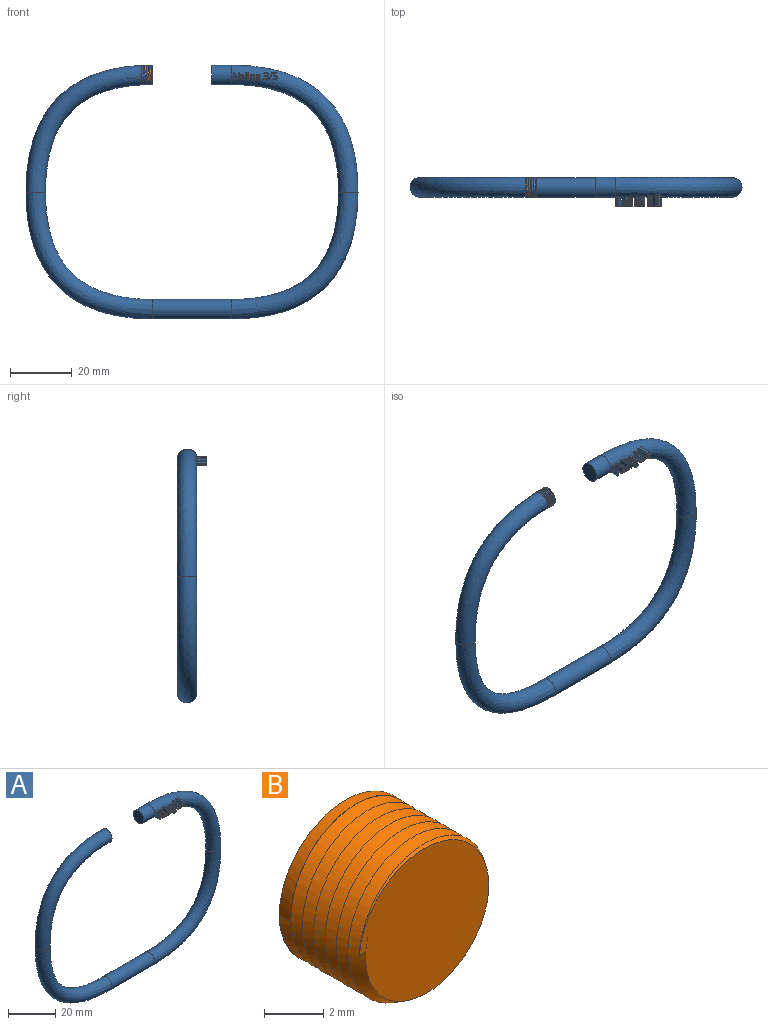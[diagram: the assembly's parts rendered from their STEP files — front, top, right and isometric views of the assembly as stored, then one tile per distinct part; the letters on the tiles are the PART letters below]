
ASSEMBLY  parts=2 mates=1
PART A: 201 faces, bbox 108x12.7x82.6 mm
  f0: bspline ~41.28x41.28mm, area 1222.4mm2, adj f3,f4,f12,f13,f14,f15,f16,f17
  f1: plane 6.35x6.35mm, normal (-1,0,0), area 31.7mm2, adj f3
  f2: plane 6.35x6.35mm, normal (1,0,0), area 31.7mm2, adj f7
  f3: cylinder r=3.17mm len=6.35mm, axis (1,0,0), area 126.7mm2, adj f0,f1
  f4: bspline ~41.28x41.28mm, area 1233.9mm2, adj f0,f5
  f5: cylinder r=3.17mm len=25.4mm, axis (-1,0,0), area 506.7mm2, adj f4,f6
  f6: bspline ~41.28x41.28mm, area 1233.9mm2, adj f5,f7
  f7: bspline ~41.28x41.28mm, area 1234.2mm2, adj f2,f6
  f8: plane 3.23x0.7mm, normal (-0.94,0,-0.35), area 2.4mm2, adj f9,f20,f21,f22
  f9: plane 3.23x0.73mm, normal (0,0,1), area 2.4mm2, adj f8,f10,f21,f22
  f10: plane 3.23x0.7mm, normal (0.94,0,-0.35), area 2.4mm2, adj f9,f11,f21,f22
  f11: extruded ~3.21x0.33mm, area 1.1mm2, adj f10,f20,f21,f22
  f12: plane 3.58x0.73mm, normal (-0.93,0,-0.36), area 2.6mm2, adj f0,f13,f19,f21
  f13: plane 3.57x0.27mm, normal (0,0,-1), area 1mm2, adj f0,f12,f14,f21
  f14: plane 3.56x2.27mm, normal (0.93,0,0.36), area 8mm2, adj f0,f13,f15,f21
  f15: plane 3.26x0.22mm, normal (0,0,1), area 0.7mm2, adj f0,f14,f16,f21
  f16: plane 3.58x2.27mm, normal (-0.93,0,0.37), area 8mm2, adj f0,f15,f17,f21
  f17: plane 3.58x0.27mm, normal (0,0,-1), area 1mm2, adj f0,f16,f18,f21
  f18: plane 3.58x0.72mm, normal (0.93,0,-0.36), area 2.6mm2, adj f0,f17,f19,f21
  f19: plane 3.29x0.91mm, normal (0,0,-1), area 3mm2, adj f0,f12,f18,f21
  f20: extruded ~3.21x0.33mm, area 1.1mm2, adj f8,f11,f21,f22
  f21: plane 2.27x2.01mm, normal (0,-1,0), area 1.3mm2, adj f8,f9,f10,f11,f12,f13,f14,f15
  f22: bspline ~6.4x6.35mm, area 0.4mm2, adj f8,f9,f10,f11,f20
  f23: plane 3.56x0.26mm, normal (0,0,-1), area 0.9mm2, adj f0,f24,f26,f27
  f24: plane 3.55x1.7mm, normal (1,0,0), area 5.6mm2, adj f0,f23,f25,f27
  f25: plane 3.18x0.26mm, normal (0,0,1), area 0.8mm2, adj f0,f24,f26,f27
  f26: plane 3.56x1.7mm, normal (-1,0,0), area 5.6mm2, adj f0,f23,f25,f27
  f27: plane 1.7x0.26mm, normal (0,-1,0), area 0.4mm2, adj f23,f24,f25,f26
  f28: extruded ~3.27x0.13mm, area 0.5mm2, adj f0,f29,f35,f36
  f29: extruded ~3.24x0.13mm, area 0.5mm2, adj f0,f28,f30,f36
  f30: extruded ~3.22x0.11mm, area 0.4mm2, adj f0,f29,f31,f36
  f31: extruded ~3.22x0.11mm, area 0.4mm2, adj f0,f30,f32,f36
  f32: extruded ~3.24x0.13mm, area 0.5mm2, adj f0,f31,f33,f36
  f33: extruded ~3.27x0.13mm, area 0.5mm2, adj f0,f32,f34,f36
  f34: extruded ~3.28x0.11mm, area 0.4mm2, adj f0,f33,f35,f36
  f35: extruded ~3.28x0.11mm, area 0.4mm2, adj f0,f28,f34,f36
  f36: plane 0.34x0.3mm, normal (0,-1,0), area 0.1mm2, adj f28,f29,f30,f31,f32,f33,f34,f35
  f37: extruded ~3.47x0.37mm, area 1.4mm2, adj f0,f38,f61,f62
  f38: extruded ~3.32x0.28mm, area 1mm2, adj f0,f37,f39,f62
  f39: extruded ~3.25x0.41mm, area 1.5mm2, adj f0,f38,f40,f62
  f40: extruded ~3.21x0.3mm, area 1mm2, adj f0,f39,f41,f62
  f41: extruded ~3.2x0.11mm, area 0.5mm2, adj f0,f40,f42,f62
  f42: extruded ~3.19x0.12mm, area 0.4mm2, adj f0,f41,f43,f62
  f43: extruded ~3.18x0.16mm, area 0.6mm2, adj f0,f42,f44,f62
  f44: extruded ~3.18x0.28mm, area 0.9mm2, adj f0,f43,f45,f62
  f45: extruded ~3.18x0.46mm, area 1.5mm2, adj f0,f44,f46,f62
  f46: plane 3.18x0.21mm, normal (0.92,0,-0.4), area 0.7mm2, adj f0,f45,f47,f62
  f47: extruded ~3.19x0.54mm, area 1.8mm2, adj f0,f46,f48,f62
  f48: extruded ~3.19x0.46mm, area 1.5mm2, adj f0,f47,f49,f62
  f49: extruded ~3.18x0.33mm, area 1.2mm2, adj f0,f48,f50,f62
  f50: extruded ~3.2x0.2mm, area 0.7mm2, adj f0,f49,f51,f62
  f51: extruded ~3.22x0.15mm, area 0.7mm2, adj f0,f50,f52,f62
  f52: extruded ~3.25x0.34mm, area 1.2mm2, adj f0,f51,f53,f62
  f53: extruded ~3.29x0.34mm, area 1.2mm2, adj f0,f52,f54,f62
  f54: extruded ~3.34x0.17mm, area 0.7mm2, adj f0,f53,f55,f62
  f55: extruded ~3.41x0.2mm, area 0.8mm2, adj f0,f54,f56,f62
  f56: extruded ~3.44x0.31mm, area 1.1mm2, adj f0,f55,f57,f62
  f57: extruded ~3.44x0.27mm, area 0.9mm2, adj f0,f56,f58,f62
  f58: extruded ~3.43x0.26mm, area 1mm2, adj f0,f57,f59,f62
  f59: plane 3.51x0.24mm, normal (-1,0,0), area 0.8mm2, adj f0,f58,f60,f62
  f60: extruded ~3.55x0.53mm, area 1.9mm2, adj f0,f59,f61,f62
  f61: extruded ~3.55x0.5mm, area 1.8mm2, adj f0,f37,f60,f62
  f62: plane 1.76x1.2mm, normal (0,-1,0), area 0.9mm2, adj f37,f38,f39,f40,f41,f42,f43,f44
  f63: plane 3.5x0.26mm, normal (0,0,-1), area 0.9mm2, adj f0,f64,f66,f67
  f64: plane 3.49x2.41mm, normal (1,0,0), area 7.8mm2, adj f0,f63,f65,f67
  f65: plane 3.35x0.26mm, normal (0,0,1), area 0.9mm2, adj f0,f64,f66,f67
  f66: plane 3.5x2.41mm, normal (-1,0,0), area 7.8mm2, adj f0,f63,f65,f67
  f67: plane 2.41x0.26mm, normal (0,-1,0), area 0.6mm2, adj f63,f64,f65,f66
  f68: plane 3.47x0.26mm, normal (0,0,-1), area 0.9mm2, adj f0,f69,f71,f72
  f69: plane 3.46x1.7mm, normal (1,0,0), area 5.5mm2, adj f0,f68,f70,f72
  f70: plane 3.2x0.26mm, normal (0,0,1), area 0.8mm2, adj f0,f69,f71,f72
  f71: plane 3.47x1.7mm, normal (-1,0,0), area 5.5mm2, adj f0,f68,f70,f72
  f72: plane 1.7x0.26mm, normal (0,-1,0), area 0.4mm2, adj f68,f69,f70,f71
  f73: extruded ~3.32x0.13mm, area 0.5mm2, adj f0,f74,f80,f81
  f74: extruded ~3.28x0.13mm, area 0.5mm2, adj f0,f73,f75,f81
  f75: extruded ~3.25x0.11mm, area 0.4mm2, adj f0,f74,f76,f81
  f76: extruded ~3.25x0.11mm, area 0.4mm2, adj f0,f75,f77,f81
  f77: extruded ~3.29x0.13mm, area 0.5mm2, adj f0,f76,f78,f81
  f78: extruded ~3.32x0.13mm, area 0.5mm2, adj f0,f77,f79,f81
  f79: extruded ~3.34x0.11mm, area 0.4mm2, adj f0,f78,f80,f81
  f80: extruded ~3.34x0.11mm, area 0.4mm2, adj f0,f73,f79,f81
  f81: plane 0.34x0.3mm, normal (0,-1,0), area 0.1mm2, adj f73,f74,f75,f76,f77,f78,f79,f80
  f82: plane 3.4x1.11mm, normal (-1,0,0), area 3.6mm2, adj f0,f83,f98,f99
  f83: plane 3.39x0.26mm, normal (0,0,-1), area 0.9mm2, adj f0,f82,f84,f99
  f84: plane 3.39x1.12mm, normal (1,0,0), area 3.6mm2, adj f0,f83,f85,f99
  f85: extruded ~3.21x0.47mm, area 1.6mm2, adj f0,f84,f86,f99
  f86: extruded ~3.22x0.46mm, area 1.6mm2, adj f0,f85,f87,f99
  f87: extruded ~3.22x0.32mm, area 1.1mm2, adj f0,f86,f88,f99
  f88: extruded ~3.21x0.22mm, area 1mm2, adj f0,f87,f89,f99
  f89: plane 3.18x0.01mm, normal (0,0,1), area 0mm2, adj f0,f88,f90,f99
  f90: plane 3.21x0.23mm, normal (0.98,0,0.18), area 0.8mm2, adj f0,f89,f91,f99
  f91: plane 3.21x0.21mm, normal (0,0,1), area 0.7mm2, adj f0,f90,f92,f99
  f92: plane 3.44x1.7mm, normal (-1,0,0), area 5.5mm2, adj f0,f91,f93,f99
  f93: plane 3.44x0.26mm, normal (0,0,-1), area 0.9mm2, adj f0,f92,f94,f99
  f94: plane 3.43x0.9mm, normal (1,0,0), area 2.9mm2, adj f0,f93,f95,f99
  f95: extruded ~3.19x0.48mm, area 1.6mm2, adj f0,f94,f96,f99
  f96: extruded ~3.19x0.39mm, area 1.4mm2, adj f0,f95,f97,f99
  f97: extruded ~3.19x0.3mm, area 1mm2, adj f0,f96,f98,f99
  f98: extruded ~3.18x0.31mm, area 1.1mm2, adj f0,f82,f97,f99
  f99: plane 1.73x1.42mm, normal (0,-1,0), area 1mm2, adj f82,f83,f84,f85,f86,f87,f88,f89
  f100: extruded ~3.18x0.27mm, area 0.9mm2, adj f101,f143,f144,f145
  f101: extruded ~3.2x0.29mm, area 1mm2, adj f100,f102,f144,f145
  f102: extruded ~3.22x0.28mm, area 1mm2, adj f101,f103,f144,f145
  f103: extruded ~3.22x0.38mm, area 2mm2, adj f102,f104,f144,f145
  f104: extruded ~3.18x0.38mm, area 1.9mm2, adj f103,f143,f144,f145
  f105: extruded ~3.56x0.21mm, area 0.9mm2, adj f106,f141,f144,f146
  f106: extruded ~3.46x0.24mm, area 0.9mm2, adj f105,f107,f144,f146
  f107: extruded ~3.36x0.27mm, area 1mm2, adj f106,f108,f144,f146
  f108: plane 3.32x0.31mm, normal (0,0,-1), area 1mm2, adj f107,f109,f144,f146
  f109: extruded ~3.31x0.32mm, area 1.1mm2, adj f108,f110,f144,f146
  f110: extruded ~3.37x0.19mm, area 0.7mm2, adj f109,f111,f144,f146
  f111: extruded ~3.49x0.26mm, area 1.1mm2, adj f110,f112,f144,f146
  f112: extruded ~3.57x0.48mm, area 1.7mm2, adj f111,f141,f144,f146
  f113: plane 3.29x0.16mm, normal (1,0,0), area 0.5mm2, adj f0,f114,f142,f144
  f114: plane 3.29x0.59mm, normal (0,0,1), area 1.9mm2, adj f0,f113,f115,f144
  f115: extruded ~3.26x0.24mm, area 0.8mm2, adj f0,f114,f116,f144
  f116: extruded ~3.26x0.47mm, area 1.6mm2, adj f0,f115,f117,f144
  f117: extruded ~3.22x0.43mm, area 1.5mm2, adj f0,f116,f118,f144
  f118: extruded ~3.18x0.3mm, area 1mm2, adj f0,f117,f119,f144
  f119: extruded ~3.19x0.21mm, area 0.9mm2, adj f0,f118,f120,f144
  f120: extruded ~3.22x0.16mm, area 0.7mm2, adj f0,f119,f121,f144
  f121: extruded ~3.25x0.16mm, area 0.6mm2, adj f0,f120,f122,f144
  f122: extruded ~3.28x0.14mm, area 0.5mm2, adj f0,f121,f123,f144
  f123: extruded ~3.3x0.11mm, area 0.5mm2, adj f0,f122,f124,f144
  f124: extruded ~3.36x0.28mm, area 1.1mm2, adj f0,f123,f125,f144
  f125: extruded ~3.48x0.27mm, area 1mm2, adj f0,f124,f126,f144
  f126: extruded ~3.66x0.35mm, area 1.5mm2, adj f0,f125,f127,f144
  f127: extruded ~3.69x0.51mm, area 2mm2, adj f0,f126,f128,f144
  f128: extruded ~3.69x0.66mm, area 2.5mm2, adj f0,f127,f129,f144
  f129: extruded ~3.55x0.43mm, area 1.8mm2, adj f0,f128,f130,f144
  f130: extruded ~3.35x0.34mm, area 1.3mm2, adj f0,f129,f131,f144
  f131: extruded ~3.26x0.42mm, area 1.5mm2, adj f0,f130,f132,f144
  f132: plane 3.26x0.3mm, normal (0,0,1), area 1mm2, adj f0,f131,f133,f144
  f133: extruded ~3.26x0.2mm, area 0.7mm2, adj f0,f132,f134,f144
  f134: extruded ~3.25x0.1mm, area 0.4mm2, adj f0,f133,f135,f144
  f135: extruded ~3.23x0.22mm, area 0.9mm2, adj f0,f134,f136,f144
  f136: extruded ~3.2x0.14mm, area 0.5mm2, adj f0,f135,f137,f144
  f137: extruded ~3.2x0.47mm, area 1.6mm2, adj f0,f136,f138,f144
  f138: extruded ~3.19x0.4mm, area 1.4mm2, adj f0,f137,f139,f144
  f139: extruded ~3.21x0.2mm, area 0.6mm2, adj f0,f138,f140,f144
  f140: extruded ~3.23x0.14mm, area 0.5mm2, adj f0,f139,f142,f144
  f141: extruded ~3.57x0.33mm, area 1.2mm2, adj f105,f112,f144,f146
  f142: plane 3.25x0.31mm, normal (0.12,0,-0.99), area 1mm2, adj f0,f113,f140,f144
  f143: extruded ~3.18x0.28mm, area 1mm2, adj f100,f104,f144,f145
  f144: plane 2.49x1.6mm, normal (0,-1,0), area 1.6mm2, adj f100,f101,f102,f103,f104,f105,f106,f107
  f145: bspline ~15.33x9.33mm, area 0.5mm2, adj f100,f101,f102,f103,f104,f143
  f146: bspline ~15.33x9.33mm, area 0.6mm2, adj f105,f106,f107,f108,f109,f110,f111,f112
  f147: extruded ~3.45x0.35mm, area 1.3mm2, adj f0,f148,f174,f175
  f148: extruded ~3.65x0.41mm, area 1.7mm2, adj f0,f147,f149,f175
  f149: extruded ~3.68x0.51mm, area 2mm2, adj f0,f148,f150,f175
  f150: extruded ~3.68x0.38mm, area 1.4mm2, adj f0,f149,f151,f175
  f151: extruded ~3.6x0.32mm, area 1.3mm2, adj f0,f150,f152,f175
  f152: plane 3.48x0.17mm, normal (-0.8,0,-0.6), area 0.7mm2, adj f0,f151,f153,f175
  f153: extruded ~3.51x0.3mm, area 1.2mm2, adj f0,f152,f154,f175
  f154: extruded ~3.55x0.28mm, area 1mm2, adj f0,f153,f155,f175
  f155: extruded ~3.55x0.31mm, area 1.2mm2, adj f0,f154,f156,f175
  f156: extruded ~3.53x0.26mm, area 1mm2, adj f0,f155,f157,f175
  f157: extruded ~3.43x0.32mm, area 1.3mm2, adj f0,f156,f158,f175
  f158: extruded ~3.3x0.42mm, area 1.5mm2, adj f0,f157,f159,f175
  f159: plane 3.25x0.23mm, normal (0,0,1), area 0.7mm2, adj f0,f158,f160,f175
  f160: plane 3.24x0.22mm, normal (-1,0,0), area 0.7mm2, adj f0,f159,f161,f175
  f161: plane 3.21x0.22mm, normal (0,0,-1), area 0.7mm2, adj f0,f160,f162,f175
  f162: extruded ~3.22x0.65mm, area 2.8mm2, adj f0,f161,f163,f175
  f163: extruded ~3.2x0.59mm, area 2.7mm2, adj f0,f162,f164,f175
  f164: extruded ~3.2x0.32mm, area 1mm2, adj f0,f163,f165,f175
  f165: extruded ~3.2x0.31mm, area 1.1mm2, adj f0,f164,f166,f175
  f166: plane 3.23x0.25mm, normal (-1,0,0), area 0.8mm2, adj f0,f165,f167,f175
  f167: extruded ~3.24x0.29mm, area 1mm2, adj f0,f166,f168,f175
  f168: extruded ~3.24x0.33mm, area 1.1mm2, adj f0,f167,f169,f175
  f169: extruded ~3.23x0.64mm, area 2.2mm2, adj f0,f168,f170,f175
  f170: extruded ~3.19x0.5mm, area 1.8mm2, adj f0,f169,f171,f175
  f171: extruded ~3.23x0.37mm, area 1.3mm2, adj f0,f170,f172,f175
  f172: extruded ~3.25x0.4mm, area 1.5mm2, adj f0,f171,f173,f175
  f173: plane 3.25x0.01mm, normal (1,0,0), area 0mm2, adj f0,f172,f174,f175
  f174: extruded ~3.31x0.34mm, area 1.3mm2, adj f0,f147,f173,f175
  f175: plane 2.33x1.48mm, normal (0,-1,0), area 1.2mm2, adj f147,f148,f149,f150,f151,f152,f153,f154
  f176: plane 3.98x2.26mm, normal (0.94,0,-0.35), area 8.2mm2, adj f0,f177,f179,f180
  f177: plane 3.98x0.26mm, normal (0,0,1), area 1mm2, adj f0,f176,f178,f180
  f178: plane 3.93x2.26mm, normal (-0.94,0,0.35), area 8.2mm2, adj f0,f177,f179,f180
  f179: plane 3.19x0.26mm, normal (0,0,-1), area 0.8mm2, adj f0,f176,f178,f180
  f180: plane 2.26x1.1mm, normal (0,-1,0), area 0.6mm2, adj f176,f177,f178,f179
  f181: extruded ~3.53x0.56mm, area 2.1mm2, adj f0,f182,f199,f200
  f182: extruded ~3.53x0.35mm, area 1.3mm2, adj f0,f181,f183,f200
  f183: plane 3.9x0.68mm, normal (1,0,-0.08), area 2.5mm2, adj f0,f182,f184,f200
  f184: plane 4.1x0.91mm, normal (0,0,-1), area 3.6mm2, adj f0,f183,f185,f200
  f185: plane 4.36x0.24mm, normal (1,0,0), area 1mm2, adj f0,f184,f186,f200
  f186: plane 4.36x1.13mm, normal (0,0,1), area 4.7mm2, adj f0,f185,f187,f200
  f187: plane 4.06x1.06mm, normal (-1,0,0.08), area 3.9mm2, adj f0,f186,f188,f200
  f188: plane 3.39x0.13mm, normal (-0.54,0,-0.84), area 0.5mm2, adj f0,f187,f189,f200
  f189: extruded ~3.43x0.39mm, area 1.3mm2, adj f0,f188,f190,f200
  f190: extruded ~3.43x0.58mm, area 2.9mm2, adj f0,f189,f191,f200
  f191: extruded ~3.31x0.37mm, area 1.4mm2, adj f0,f190,f192,f200
  f192: extruded ~3.22x0.42mm, area 1.4mm2, adj f0,f191,f193,f200
  f193: extruded ~3.19x0.32mm, area 1mm2, adj f0,f192,f194,f200
  f194: extruded ~3.19x0.27mm, area 0.9mm2, adj f0,f193,f195,f200
  f195: plane 3.19x0.25mm, normal (-1,0,0), area 0.8mm2, adj f0,f194,f196,f200
  f196: extruded ~3.18x0.58mm, area 1.9mm2, adj f0,f195,f197,f200
  f197: extruded ~3.2x0.62mm, area 2.1mm2, adj f0,f196,f198,f200
  f198: extruded ~3.34x0.55mm, area 2mm2, adj f0,f197,f199,f200
  f199: extruded ~3.52x0.49mm, area 1.9mm2, adj f0,f181,f198,f200
  f200: plane 2.29x1.42mm, normal (0,-1,0), area 1.2mm2, adj f181,f182,f183,f184,f185,f186,f187,f188
PART B: 7 faces, bbox 6.4x4.4x7.3 mm
  f0: cylinder r=3.17mm len=6.35mm, axis (0,1,0), area 5.4mm2, adj f1,f2,f3
  f1: plane 6.35x6.35mm, normal (0,1,0), area 31.7mm2, adj f0
  f2: plane 0.55x0.32mm, normal (0,0,-1), area 0.1mm2, adj f0,f3,f4,f5
  f3: bspline ~7.33x6.35mm, area 0.1mm2, adj f0,f2,f4
  f4: bspline ~7.33x6.34mm, area 77.4mm2, adj f2,f3,f5,f6
  f5: bspline ~7.33x6.34mm, area 35.7mm2, adj f2,f4,f6
  f6: plane 6.18x6.04mm, normal (0,-1,0), area 28.6mm2, adj f4,f5
PLACE A at identity
PLACE B rot(axis=(-0.58,0.58,0.58),120deg) t=(-16.51,-0.1,38.1)mm
MATE fastened B.f6 <-> A.f3  axis (1,0,0) through (-12.7,0,38.1)mm
